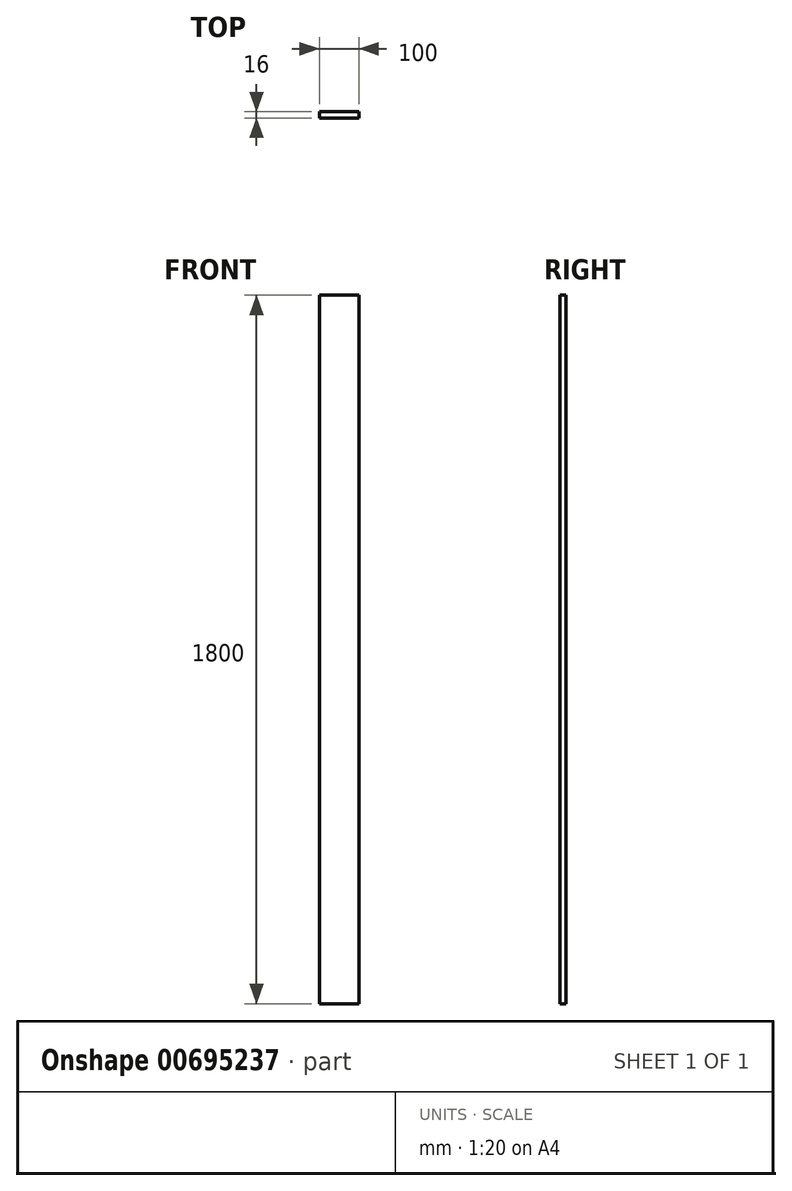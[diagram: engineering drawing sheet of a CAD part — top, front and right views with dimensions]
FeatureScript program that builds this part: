
annotation { "Feature Type Name" : "Feature", "Feature Type Description" : "" }
export const myFeature = defineFeature(function(context is Context, id is Id, definition is map)
    precondition{}
    {
        {
            var Q0;
            Q0=qCreatedBy(makeId("Front.planeOp"),FACE);
            var sketch = newSketch(context, id + "F0", { "sketchPlane" : qUnion([Q0])});
            skLineSegment(sketch, "E0.bottom", {"start": v(-88.1, 1673.3) * mm, "end": v(11.9, 1673.3) * mm});
            skLineSegment(sketch, "E0.top", {"start": v(-88.1, -126.7) * mm, "end": v(11.9, -126.7) * mm});
            skLineSegment(sketch, "E0.left", {"start": v(-88.1, 1673.3) * mm, "end": v(-88.1, -126.7) * mm});
            skLineSegment(sketch, "E0.right", {"start": v(11.9, 1673.3) * mm, "end": v(11.9, -126.7) * mm});
            skLineSegment(sketch, "E1", {"start": v(0, 1673.3) * mm, "end": v(0, -126.7) * mm, "construction": true});
            skSolve(sketch);
        }
        {
            var Q0;
            Q0=makeQuery(id+"F0.imprint","IMPRINT",FACE,{"disambiguationData":[TD([[makeQuery(id+"F0.imprint","IMPRINT",EDGE,{"derivedFrom":sQuery(id+"F0.wireOp",EDGE,"E0.bottom")}),-1.0]])]});
            extrude(context, id + "F1", {"entities" : qUnion([Q0]), "depth" : 16 * mm, "offsetDistance" : 25 * mm});
        }
    });
